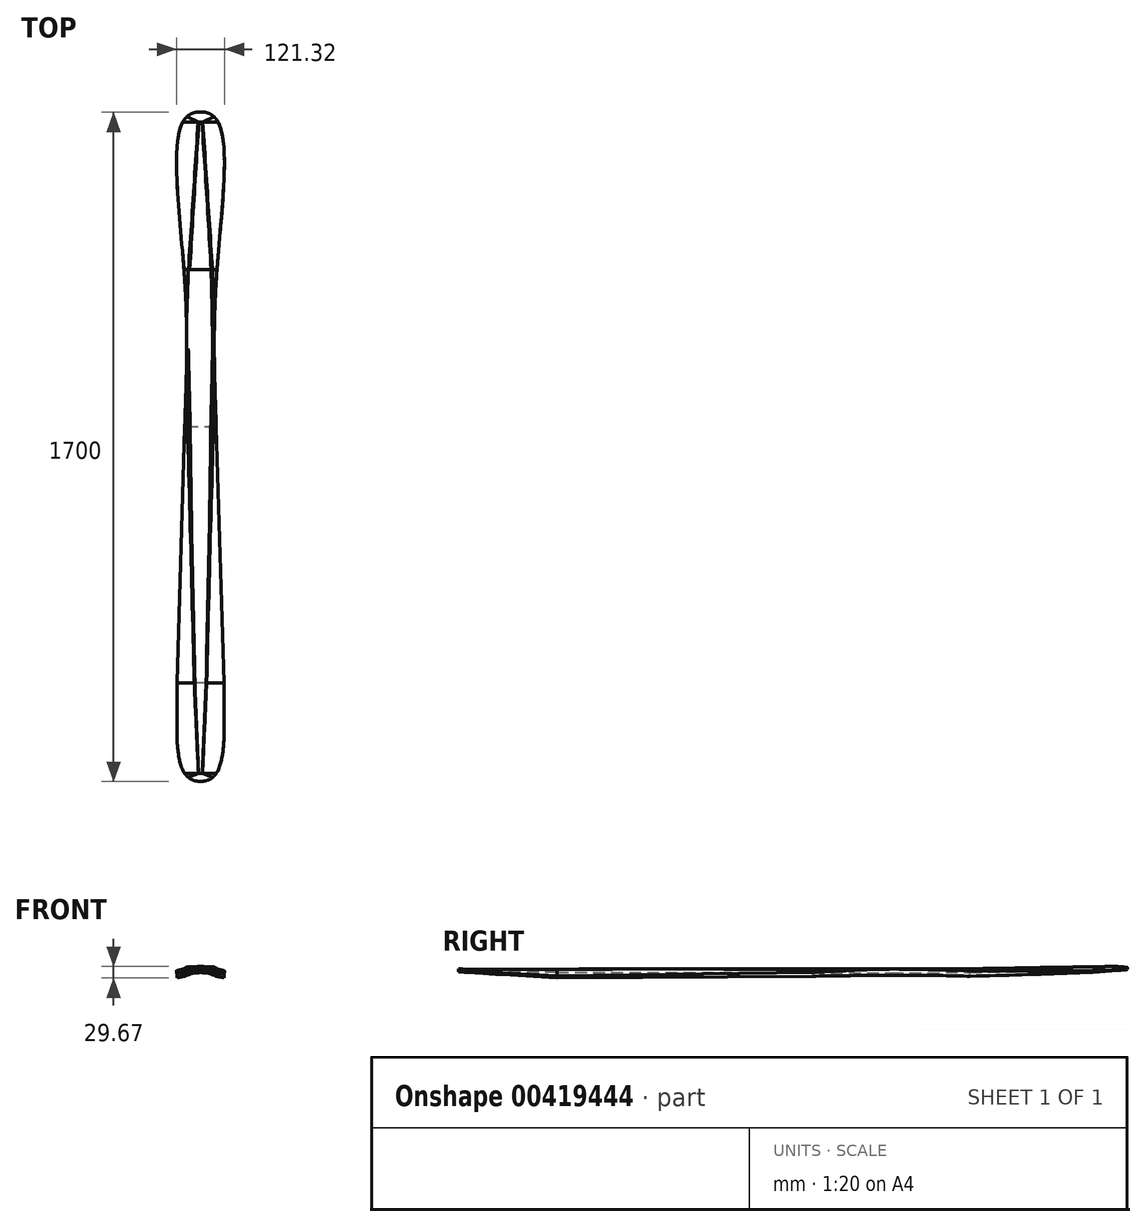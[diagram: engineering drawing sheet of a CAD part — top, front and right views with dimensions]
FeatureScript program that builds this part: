
annotation { "Feature Type Name" : "Feature", "Feature Type Description" : "" }
export const myFeature = defineFeature(function(context is Context, id is Id, definition is map)
    precondition{}
    {
        {
            var Q0;
            Q0=qCreatedBy(makeId("Front.planeOp"),FACE);
            cPlane(context, id + "F0", {"entities" : qUnion([Q0]), "cplaneType" : CPlaneType.OFFSET, "offset" : 200 * mm, "width" : 150 * mm, "height" : 150 * mm});
        }
        {
            var Q0;
            Q0=qCreatedBy(makeId("Front.planeOp"),FACE);
            cPlane(context, id + "F1", {"entities" : qUnion([Q0]), "cplaneType" : CPlaneType.OFFSET, "offset" : 200 * mm, "oppositeDirection" : true, "width" : 150 * mm, "height" : 150 * mm});
        }
        {
            var Q0;
            Q0=qCreatedBy(id+"F0.planeOp",FACE);
            cPlane(context, id + "F2", {"entities" : qUnion([Q0]), "cplaneType" : CPlaneType.OFFSET, "offset" : 650 * mm, "width" : 150 * mm, "height" : 150 * mm});
        }
        {
            var Q0;
            Q0=qCreatedBy(id+"F2.planeOp",FACE);
            cPlane(context, id + "F3", {"entities" : qUnion([Q0]), "cplaneType" : CPlaneType.OFFSET, "offset" : 230 * mm, "width" : 150 * mm, "height" : 150 * mm});
        }
        {
            var Q0;
            Q0=qCreatedBy(id+"F3.planeOp",FACE);
            cPlane(context, id + "F4", {"entities" : qUnion([Q0]), "cplaneType" : CPlaneType.OFFSET, "offset" : 20 * mm, "width" : 150 * mm, "height" : 150 * mm});
        }
        {
            var Q0;
            Q0=qCreatedBy(id+"F1.planeOp",FACE);
            cPlane(context, id + "F5", {"entities" : qUnion([Q0]), "cplaneType" : CPlaneType.OFFSET, "offset" : 375 * mm, "oppositeDirection" : true, "width" : 150 * mm, "height" : 150 * mm});
        }
        {
            var Q0;
            Q0=qCreatedBy(id+"F5.planeOp",FACE);
            cPlane(context, id + "F6", {"entities" : qUnion([Q0]), "cplaneType" : CPlaneType.OFFSET, "offset" : 25 * mm, "oppositeDirection" : true, "width" : 150 * mm, "height" : 150 * mm});
        }
        {
            var Q0;
            Q0=qCreatedBy(makeId("Front.planeOp"),FACE);
            var sketch = newSketch(context, id + "F7", { "sketchPlane" : qUnion([Q0])});
            skLineSegment(sketch, "E0.bottom", {"start": v(-35, 9) * mm, "end": v(35, 9) * mm});
            skLineSegment(sketch, "E0.left", {"start": v(-40, 4) * mm, "end": v(-40, -10) * mm});
            skLineSegment(sketch, "E0.right", {"start": v(40, 4) * mm, "end": v(40, -10) * mm});
            skArc(sketch, "E1", {"start": v(40, -10) * mm, "mid": v(0, -1) * mm, "end": v(-40, -10) * mm});
            skLineSegment(sketch, "E2", {"start": v(-40, 4) * mm, "end": v(-35, 9) * mm});
            skLineSegment(sketch, "E3", {"start": v(35, 9) * mm, "end": v(40, 4) * mm});
            skSolve(sketch);
        }
        {
            var Q0;
            Q0=qCreatedBy(makeId("Top.planeOp"),FACE);
            var sketch = newSketch(context, id + "F8", { "sketchPlane" : qUnion([Q0])});
            skLineSegment(sketch, "E4", {"start": v(0, 600) * mm, "end": v(0, -1100) * mm});
            skLineSegment(sketch, "E5", {"start": v(0, 600) * mm, "end": v(-10, 600) * mm});
            skFitSpline(sketch, "E6", {"points": [v(-10, 600) * mm, v(-45, 575) * mm, v(-42, 200) * mm, v(-40, -200) * mm, v(-60, -850) * mm, v(-40, -1080) * mm, v(0, -1100) * mm], "startDerivative": vector(-311.77, 0) * mm, "endDerivative": vector(627.87, 0) * mm});
            skLineSegment(sketch, "E7.MirrorCS", {"start": v(0, 600) * mm, "end": v(10, 600) * mm});
            skFitSpline(sketch, "E8.MirrorCS", {"points": [v(10, 600) * mm, v(45, 575) * mm, v(42, 200) * mm, v(40, -200) * mm, v(60, -850) * mm, v(40, -1080) * mm, v(0, -1100) * mm], "startDerivative": vector(311.77, 0) * mm, "endDerivative": vector(-627.87, 0) * mm});
            skLineSegment(sketch, "E9.bottom", {"start": v(-715.09, 749.37) * mm, "end": v(821.3, 749.37) * mm});
            skLineSegment(sketch, "E9.top", {"start": v(-715.09, -1266.26) * mm, "end": v(821.3, -1266.26) * mm});
            skLineSegment(sketch, "E9.left", {"start": v(-715.09, 749.37) * mm, "end": v(-715.09, -1266.26) * mm});
            skLineSegment(sketch, "E9.right", {"start": v(821.3, 749.37) * mm, "end": v(821.3, -1266.26) * mm});
            skSolve(sketch);
        }
        {
            var Q0;
            Q0=qCreatedBy(id+"F0.planeOp",FACE);
            var sketch = newSketch(context, id + "F9", { "sketchPlane" : qUnion([Q0])});
            skLineSegment(sketch, "E10", {"start": v(-40, 0) * mm, "end": v(-30, 9) * mm});
            skLineSegment(sketch, "E11", {"start": v(-40, 0) * mm, "end": v(-40, -10) * mm});
            skLineSegment(sketch, "E12.MirrorCS", {"start": v(40, 0) * mm, "end": v(40, -10) * mm});
            skLineSegment(sketch, "E13.MirrorCS", {"start": v(40, 0) * mm, "end": v(30, 9) * mm});
            skLineSegment(sketch, "E14", {"start": v(-30, 9) * mm, "end": v(30, 9) * mm});
            skArc(sketch, "E15", {"start": v(40, -10) * mm, "mid": v(0, -0.85) * mm, "end": v(-40, -10) * mm});
            skSolve(sketch);
        }
        {
            var Q0;
            Q0=qCreatedBy(id+"F2.planeOp",FACE);
            var sketch = newSketch(context, id + "F10", { "sketchPlane" : qUnion([Q0])});
            skArc(sketch, "E16", {"start": v(60, -14.67) * mm, "mid": v(0, 0) * mm, "end": v(-60, -14.67) * mm});
            skArc(sketch, "E17", {"start": v(60, -8.8) * mm, "mid": v(38.43, 2.07) * mm, "end": v(15, 7.97) * mm});
            skLineSegment(sketch, "E18", {"start": v(-60, -8.8) * mm, "end": v(-60, -14.67) * mm});
            skLineSegment(sketch, "E19", {"start": v(60, -8.8) * mm, "end": v(60, -14.67) * mm});
            skLineSegment(sketch, "E20", {"start": v(-15, 7.97) * mm, "end": v(15, 7.97) * mm});
            skArc(sketch, "E21.trimOffspring", {"start": v(-15, 7.97) * mm, "mid": v(-38.43, 2.07) * mm, "end": v(-60, -8.8) * mm});
            skSolve(sketch);
        }
        {
            var Q0;
            Q0=qCreatedBy(id+"F3.planeOp",FACE);
            var sketch = newSketch(context, id + "F11", { "sketchPlane" : qUnion([Q0])});
            skLineSegment(sketch, "E22.bottom", {"start": v(-5, 8) * mm, "end": v(5, 8) * mm});
            skLineSegment(sketch, "E22.top", {"start": v(-60, 0) * mm, "end": v(60, 0) * mm});
            skLineSegment(sketch, "E22.left", {"start": v(-60, 4) * mm, "end": v(-60, 0) * mm});
            skLineSegment(sketch, "E22.right", {"start": v(60, 4) * mm, "end": v(60, 0) * mm});
            skPoint(sketch, "E23", {"position": v(-5, 8) * mm});
            skPoint(sketch, "E24", {"position": v(5, 8) * mm});
            skLineSegment(sketch, "E25", {"start": v(5, 8) * mm, "end": v(60, 4) * mm});
            skLineSegment(sketch, "E26", {"start": v(-60, 4) * mm, "end": v(-5, 8) * mm});
            skSolve(sketch);
        }
        {
            var Q0;
            Q0=qCreatedBy(id+"F4.planeOp",FACE);
            var sketch = newSketch(context, id + "F12", { "sketchPlane" : qUnion([Q0])});
            skLineSegment(sketch, "E27.bottom", {"start": v(-60, 8.5) * mm, "end": v(60, 8.5) * mm});
            skLineSegment(sketch, "E27.top", {"start": v(-45, 1.5) * mm, "end": v(45, 1.5) * mm});
            skLineSegment(sketch, "E27.left", {"start": v(-60, 8.5) * mm, "end": v(-60, 5) * mm});
            skLineSegment(sketch, "E27.right", {"start": v(60, 8.5) * mm, "end": v(60, 5) * mm});
            skLineSegment(sketch, "E28", {"start": v(-60, 5) * mm, "end": v(-45, 1.5) * mm});
            skLineSegment(sketch, "E29", {"start": v(60, 5) * mm, "end": v(45, 1.5) * mm});
            skSolve(sketch);
        }
        {
            var Q0;
            Q0=qCreatedBy(id+"F1.planeOp",FACE);
            var sketch = newSketch(context, id + "F13", { "sketchPlane" : qUnion([Q0])});
            skLineSegment(sketch, "E30", {"start": v(42, -10) * mm, "end": v(42, 4) * mm});
            skLineSegment(sketch, "E31", {"start": v(42, 4) * mm, "end": v(29, 9) * mm});
            skLineSegment(sketch, "E32", {"start": v(29, 9) * mm, "end": v(-29, 9) * mm});
            skLineSegment(sketch, "E33", {"start": v(-29, 9) * mm, "end": v(-42, 4) * mm});
            skLineSegment(sketch, "E34", {"start": v(-42, 4) * mm, "end": v(-42, -10) * mm});
            skArc(sketch, "E35", {"start": v(42, -10) * mm, "mid": v(0, -0.75) * mm, "end": v(-42, -10) * mm});
            skSolve(sketch);
        }
        {
            var Q0;
            Q0=qCreatedBy(id+"F5.planeOp",FACE);
            var sketch = newSketch(context, id + "F14", { "sketchPlane" : qUnion([Q0])});
            skLineSegment(sketch, "E36.left", {"start": v(75, 2) * mm, "end": v(75, 0) * mm});
            skLineSegment(sketch, "E36.right", {"start": v(-75, 2) * mm, "end": v(-75, 0) * mm});
            skArc(sketch, "E37", {"start": v(75, 0) * mm, "mid": v(0, 7.1) * mm, "end": v(-75, 0) * mm});
            skLineSegment(sketch, "E38", {"start": v(75, 2) * mm, "end": v(5, 15) * mm});
            skLineSegment(sketch, "E39", {"start": v(5, 15) * mm, "end": v(-5, 15) * mm});
            skLineSegment(sketch, "E40", {"start": v(-5, 15) * mm, "end": v(-75, 2) * mm});
            skSolve(sketch);
        }
        {
            var Q0;
            Q0=qCreatedBy(id+"F6.planeOp",FACE);
            var sketch = newSketch(context, id + "F15", { "sketchPlane" : qUnion([Q0])});
            skLineSegment(sketch, "E41.bottom", {"start": v(60, 12) * mm, "end": v(-60, 12) * mm});
            skLineSegment(sketch, "E41.left", {"start": v(70, 8) * mm, "end": v(70, 4) * mm});
            skLineSegment(sketch, "E41.right", {"start": v(-70, 8) * mm, "end": v(-70, 4) * mm});
            skArc(sketch, "E42", {"start": v(70, 4) * mm, "mid": v(0, 7.07) * mm, "end": v(-70, 4) * mm});
            skLineSegment(sketch, "E43", {"start": v(70, 8) * mm, "end": v(60, 12) * mm});
            skLineSegment(sketch, "E44", {"start": v(-70, 8) * mm, "end": v(-60, 12) * mm});
            skSolve(sketch);
        }
        {
            var Q0;
            Q0 = qSketchRegion(id + "F7", true);
            var Q1;
            Q1 = qSketchRegion(id + "F9", true);
            loft(context, id + "F16", {"sheetProfilesArray" : [{ "sheetProfileEntities" : qUnion([Q0]) }, { "sheetProfileEntities" : qUnion([Q1]) }]});
        }
        {
            var Q1;
            Q1 = qSketchRegion(id + "F9", true);
            var Q2;
            Q2 = qSketchRegion(id + "F10", true);
            loft(context, id + "F17", {"operationType" : NewBodyOperationType.ADD, "sheetProfilesArray" : [{ "sheetProfileEntities" : qUnion([Q1]) }, { "sheetProfileEntities" : qUnion([Q2]) }]});
        }
        {
            var Q1;
            Q1 = qSketchRegion(id + "F10", true);
            var Q2;
            Q2 = qSketchRegion(id + "F11", true);
            loft(context, id + "F18", {"operationType" : NewBodyOperationType.ADD, "sheetProfilesArray" : [{ "sheetProfileEntities" : qUnion([Q1]) }, { "sheetProfileEntities" : qUnion([Q2]) }]});
        }
        {
            var Q1;
            Q1 = qSketchRegion(id + "F11", true);
            var Q2;
            Q2 = qSketchRegion(id + "F12", true);
            loft(context, id + "F19", {"operationType" : NewBodyOperationType.ADD, "sheetProfilesArray" : [{ "sheetProfileEntities" : qUnion([Q1]) }, { "sheetProfileEntities" : qUnion([Q2]) }]});
        }
        {
            var Q1;
            Q1 = qSketchRegion(id + "F7", true);
            var Q2;
            Q2 = qSketchRegion(id + "F13", true);
            loft(context, id + "F20", {"operationType" : NewBodyOperationType.ADD, "sheetProfilesArray" : [{ "sheetProfileEntities" : qUnion([Q1]) }, { "sheetProfileEntities" : qUnion([Q2]) }]});
        }
        {
            var Q1;
            Q1 = qSketchRegion(id + "F13", true);
            var Q2;
            Q2 = qSketchRegion(id + "F14", true);
            loft(context, id + "F21", {"operationType" : NewBodyOperationType.ADD, "sheetProfilesArray" : [{ "sheetProfileEntities" : qUnion([Q1]) }, { "sheetProfileEntities" : qUnion([Q2]) }]});
        }
        {
            var Q1;
            Q1 = qSketchRegion(id + "F14", true);
            var Q2;
            Q2 = qSketchRegion(id + "F15", true);
            loft(context, id + "F22", {"operationType" : NewBodyOperationType.ADD, "sheetProfilesArray" : [{ "sheetProfileEntities" : qUnion([Q1]) }, { "sheetProfileEntities" : qUnion([Q2]) }]});
        }
        {
            var Q0;
            Q0=makeQuery(id+"F8.imprint","IMPRINT",FACE,{"disambiguationData":[TD([[makeQuery(id+"F8.imprint","IMPRINT",EDGE,{"derivedFrom":sQuery(id+"F8.wireOp",EDGE,"E5")}),-1.0]])]});
            extrude(context, id + "F23", {"entities" : qUnion([Q0]), "operationType" : NewBodyOperationType.REMOVE, "endBound" : BoundingType.SYMMETRIC, "oppositeDirection" : true, "depth" : 400 * mm});
        }
        {
            var Q0;
            Q0=makeQuery(id+"F17.opLoft","SWEPT_EDGE",EDGE,{"disambiguationData":[OSD([sQuery(id+"F9.wireOp",EDGE,"E13.MirrorCS"),sQuery(id+"F9.wireOp",EDGE,"E14"),sQuery(id+"F10.wireOp",EDGE,"E17"),sQuery(id+"F10.wireOp",EDGE,"E20")])]});
            var Q1;
            Q1=makeQuery(id+"F17.opLoft","SWEPT_EDGE",EDGE,{"disambiguationData":[OSD([sQuery(id+"F9.wireOp",EDGE,"E10"),sQuery(id+"F9.wireOp",EDGE,"E14"),sQuery(id+"F10.wireOp",EDGE,"E20"),sQuery(id+"F10.wireOp",EDGE,"E21.trimOffspring")])]});
            var Q2;
            Q2=makeQuery(id+"F18.opLoft","SWEPT_EDGE",EDGE,{"disambiguationData":[OSD([sQuery(id+"F10.wireOp",EDGE,"E20"),sQuery(id+"F10.wireOp",EDGE,"E21.trimOffspring"),sQuery(id+"F11.wireOp",EDGE,"E22.bottom"),sQuery(id+"F11.wireOp",EDGE,"E26")])]});
            var Q3;
            Q3=makeQuery(id+"F18.opLoft","SWEPT_EDGE",EDGE,{"disambiguationData":[OSD([sQuery(id+"F10.wireOp",EDGE,"E17"),sQuery(id+"F10.wireOp",EDGE,"E20"),sQuery(id+"F11.wireOp",EDGE,"E22.bottom"),sQuery(id+"F11.wireOp",EDGE,"E25")])]});
            var Q4;
            Q4=makeQuery(id+"F21.opLoft","SWEPT_EDGE",EDGE,{"disambiguationData":[OSD([sQuery(id+"F13.wireOp",EDGE,"E31"),sQuery(id+"F13.wireOp",EDGE,"E32"),sQuery(id+"F14.wireOp",EDGE,"E38"),sQuery(id+"F14.wireOp",EDGE,"E39")])]});
            var Q5;
            Q5=makeQuery(id+"F21.opLoft","SWEPT_EDGE",EDGE,{"disambiguationData":[OSD([sQuery(id+"F13.wireOp",EDGE,"E32"),sQuery(id+"F13.wireOp",EDGE,"E33"),sQuery(id+"F14.wireOp",EDGE,"E39"),sQuery(id+"F14.wireOp",EDGE,"E40")])]});
            var Q6;
            Q6=makeQuery(id+"F20.opLoft","SWEPT_EDGE",EDGE,{"disambiguationData":[OSD([sQuery(id+"F7.wireOp",EDGE,"E0.bottom"),sQuery(id+"F7.wireOp",EDGE,"E3"),sQuery(id+"F13.wireOp",EDGE,"E31"),sQuery(id+"F13.wireOp",EDGE,"E32")])]});
            var Q7;
            Q7=makeQuery(id+"F20.opLoft","SWEPT_EDGE",EDGE,{"disambiguationData":[OSD([sQuery(id+"F7.wireOp",EDGE,"E0.bottom"),sQuery(id+"F7.wireOp",EDGE,"E2"),sQuery(id+"F13.wireOp",EDGE,"E32"),sQuery(id+"F13.wireOp",EDGE,"E33")])]});
            var Q8;
            Q8=makeQuery(id+"F16.opLoft","SWEPT_EDGE",EDGE,{"disambiguationData":[OSD([sQuery(id+"F7.wireOp",EDGE,"E0.bottom"),sQuery(id+"F7.wireOp",EDGE,"E2"),sQuery(id+"F9.wireOp",EDGE,"E10"),sQuery(id+"F9.wireOp",EDGE,"E14")])]});
            var Q9;
            Q9=makeQuery(id+"F16.opLoft","SWEPT_EDGE",EDGE,{"disambiguationData":[OSD([sQuery(id+"F7.wireOp",EDGE,"E0.bottom"),sQuery(id+"F7.wireOp",EDGE,"E3"),sQuery(id+"F9.wireOp",EDGE,"E13.MirrorCS"),sQuery(id+"F9.wireOp",EDGE,"E14")])]});
            fillet(context, id + "F24", {"entities" : qUnion([Q0, Q1, Q2, Q3, Q4, Q5, Q6, Q7, Q8, Q9]), "radius" : 10 * mm, "tangentPropagation" : true, "allowEdgeOverflow" : false});
        }
    });
